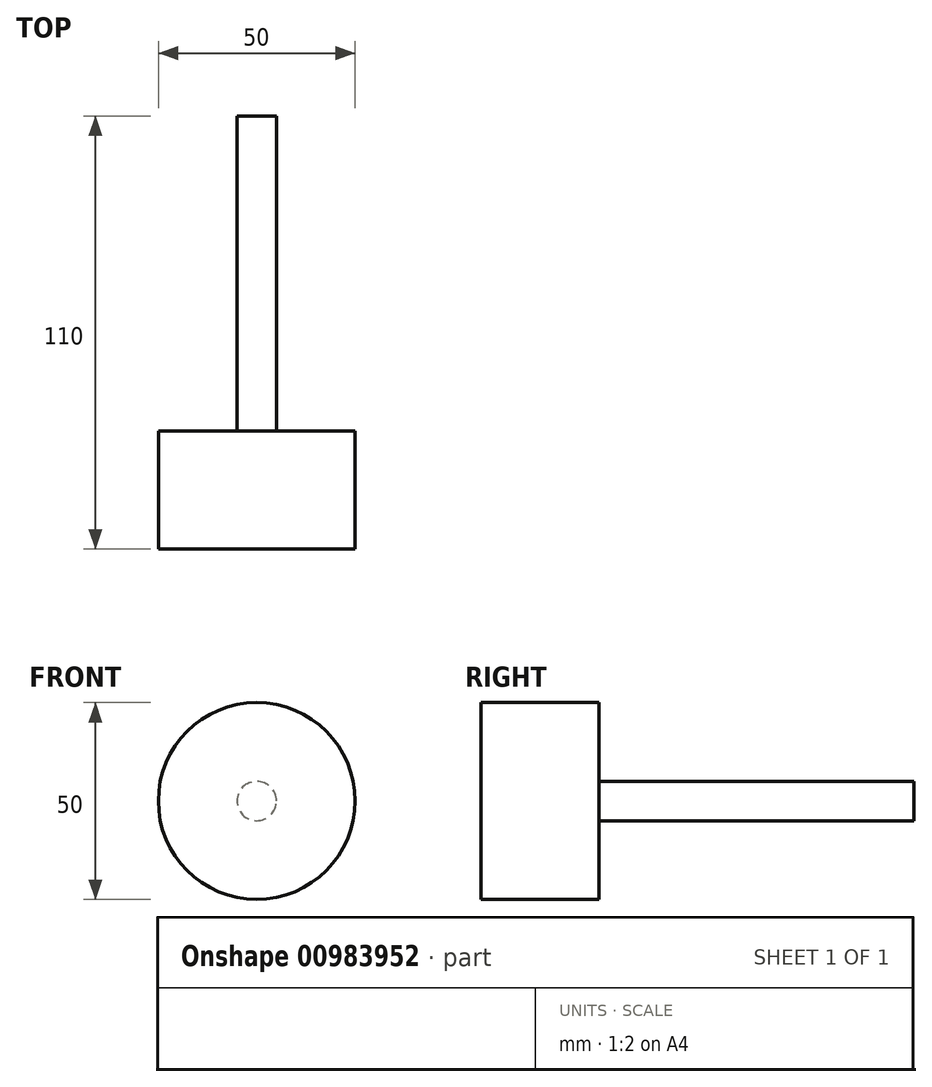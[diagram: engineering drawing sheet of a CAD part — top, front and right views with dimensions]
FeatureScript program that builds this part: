
annotation { "Feature Type Name" : "Feature", "Feature Type Description" : "" }
export const myFeature = defineFeature(function(context is Context, id is Id, definition is map)
    precondition{}
    {
        {
            var Q0;
            Q0=qCreatedBy(makeId("Front.planeOp"),FACE);
            var sketch = newSketch(context, id + "F0", { "sketchPlane" : qUnion([Q0])});
            skCircle(sketch, "E0", {"center": v(0, 0) * mm, "radius": 5 * mm});
            skSolve(sketch);
        }
        {
            var Q0;
            Q0=makeQuery(id+"F0.imprint","IMPRINT",FACE,{"disambiguationData":[TD([[makeQuery(id+"F0.imprint","IMPRINT",EDGE,{"derivedFrom":sQuery(id+"F0.wireOp",EDGE,"E0")}),1.0]])]});
            extrude(context, id + "F1", {"entities" : qUnion([Q0]), "oppositeDirection" : true, "depth" : 80 * mm, "offsetDistance" : 25 * mm});
        }
        {
            var Q0;
            Q0=makeQuery(id+"F1.opExtrude","CAP_FACE",FACE,{"disambiguationData":[OSD([sQuery(id+"F0.wireOp",EDGE,"E0")])],"isStart":true});
            cPlane(context, id + "F2", {"entities" : qUnion([Q0]), "cplaneType" : CPlaneType.OFFSET, "offset" : 0 * mm, "width" : 150 * mm, "height" : 150 * mm});
        }
        {
            var Q0;
            Q0=qCreatedBy(id+"F2.planeOp",FACE);
            var sketch = newSketch(context, id + "F3", { "sketchPlane" : qUnion([Q0])});
            skCircle(sketch, "E1", {"center": v(0, 0) * mm, "radius": 25 * mm});
            skSolve(sketch);
        }
        {
            var Q0;
            Q0=makeQuery(id+"F3.imprint","IMPRINT",FACE,{"disambiguationData":[TD([[makeQuery(id+"F3.imprint","IMPRINT",EDGE,{"derivedFrom":sQuery(id+"F3.wireOp",EDGE,"E1")}),1.0]])]});
            extrude(context, id + "F4", {"entities" : qUnion([Q0]), "operationType" : NewBodyOperationType.ADD, "depth" : 30 * mm, "offsetDistance" : 25 * mm});
        }
    });
